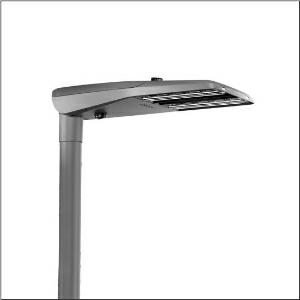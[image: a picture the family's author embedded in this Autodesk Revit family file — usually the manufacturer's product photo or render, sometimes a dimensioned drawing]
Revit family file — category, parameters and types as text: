
# Revit family: streetlight_sl_11_iq_midi___st1_2p1_0_5xc3g51y08me_d530
name_source: partatom
category: Lighting Fixtures
units: mm (PartAtom-declared; Revit-internal decimal feet)

## family parameters
Cut with Voids When Loaded = No
Host = Face
Light Source = No
Part Type = Normal
Room Calculation Point = No
Round Connector Dimension = Use Diameter
Shared = No

## types (1)
- --- (1 x LED, 17750 lm, 119.8 W, 3000K)
    Apparent Load = 120 VA
    CIE Flux Codes = 31 68 95 100 100
    Color Rendering = 70
    Color Temperature = 3000K
    Default Elevation = 1800 mm
    Description = Streetlight SL 11 iQ midi, mast luminaire, primary light control with 3 zone facetted reflector, of plastic, silver coated, highly specular, primary optical cover: cover, of PMMA, transparent, light distribution: ST1.2P1.0, light emission: direct distribution, primary light characteristic: asymmetric, installation type: post-top, side-entry, lamps: LED, High Power LED, rated values: 17.750lm | 119,8W | 148,2lm/W (begin service life); end service life: 17.750lm | 126,7W; at 50% lumin. flux: 8.875lm | 54,9W | 161,7lm/W, colour temperature: 3000K, colour rendering: CRI > 70, light colour: 730, light setting 1 begin service life: 100% | 17.750lm | 119,8W | 148,2lm/W | 3.000K, light setting 1 end service life: 126,7W, further light settings possible, control: pre-setting: logarithmic dimming characteristic, Street-Remote, Auto-Match, Temp-Guard, Lumen-Switch, Night-Set, Smart-Wire, Light-Fading, Desk-Remote (wireless, voltage-free reading and setting of iQ features in the workshop via application-optimized NFC function/RFID function), optimised constant luminous flux control (CLO 2.0), with cable H07RN-F 3x 1.5mm², mains connection: 230..240V, AC, 50/60Hz, connection cable pre-assembled, cable length: 12,5m, luminaire housing, of diecast aluminium, powder-coated, SITECO metallic grey (DB 702S), please order mast flange separately, inclination adjustable without tools: 0°, 5°, 10°, 15° (post-top) | 0°, -5°, -10°, -15° (side-entry), sealing non-destructively replaceable, multi-level sealing system, length: 780mm, width: 376mm, height: 118mm, mast flange for spigot size: 42mm (side-entry): 5XC10008XM4, 60/48mm (side-entry/post-top): 5XC10108XM2, 76/60mm (side-entry/post-top): 5XC10108XM1, equipment: Power, Smart Interface below and above, protection rating (complete): IP66, insulation class (complete): insulation class II (safety insulation), certification: CE, ENEC, ENEC+, VDE, UKCA, impact resistance: IK10, permissible operating ambient temperature for outdoor applications: -25..+50°C, standard-compliant lighting for roads and squares, Environmental Product Declaration (EPD) tested and certified by an independent institute, packaging unit: 1 piece

Light Distribution: ST1.2P1.0
    Height = 118 mm
    Lamp = 1 x LED
    Lamp Light Flux = 17750 lm
    Lamp Power = 119.8 W
    Lamp count = 1
    Length = 780 mm
    Luminous efficacy = 148 lm/W
    Manufacturer = Siteco
    ModVariant = No
    Model = 5XC3G51Y08ME
    Number of Poles = 1
    OnlyDefault = Yes
    Power Factor = 1
    Product Name = Streetlight SL 11 iQ midi | ST1.2P1.0
    Product group = mast luminaire | pylon top
    ProductGroupID = 6100
    Protection Class = Protection class II
    Protection Degree = IP 66
    RLX_Detail_Level = 1
    RLX_Emergency_Light_Flux = 0 lm
    RLX_Emergency_Type = 0
    RLX_Emergency_Type_DB = No
    RlxData = <blob elided: 69877 chars, md5=b09ba980>
    Socket = socket
    Standby Power = 0 W
    System Light Flux = 17750 lm
    System Power = 120 W
    Type Comments = factory setting: luminous flux: 100 % | dim-lin: 254 | 540 mA
    Type Image = l_1004429.jpg
    URL = http://relux.com
    VarID = @adj_044093
    Voltage = 0 V
    Weight = 0.00 kg
    Width = 376 mm

## geometry (parser evidence)
native form markers: Blend x4, Sweep x9
no freeform markers — native parametric forms only
